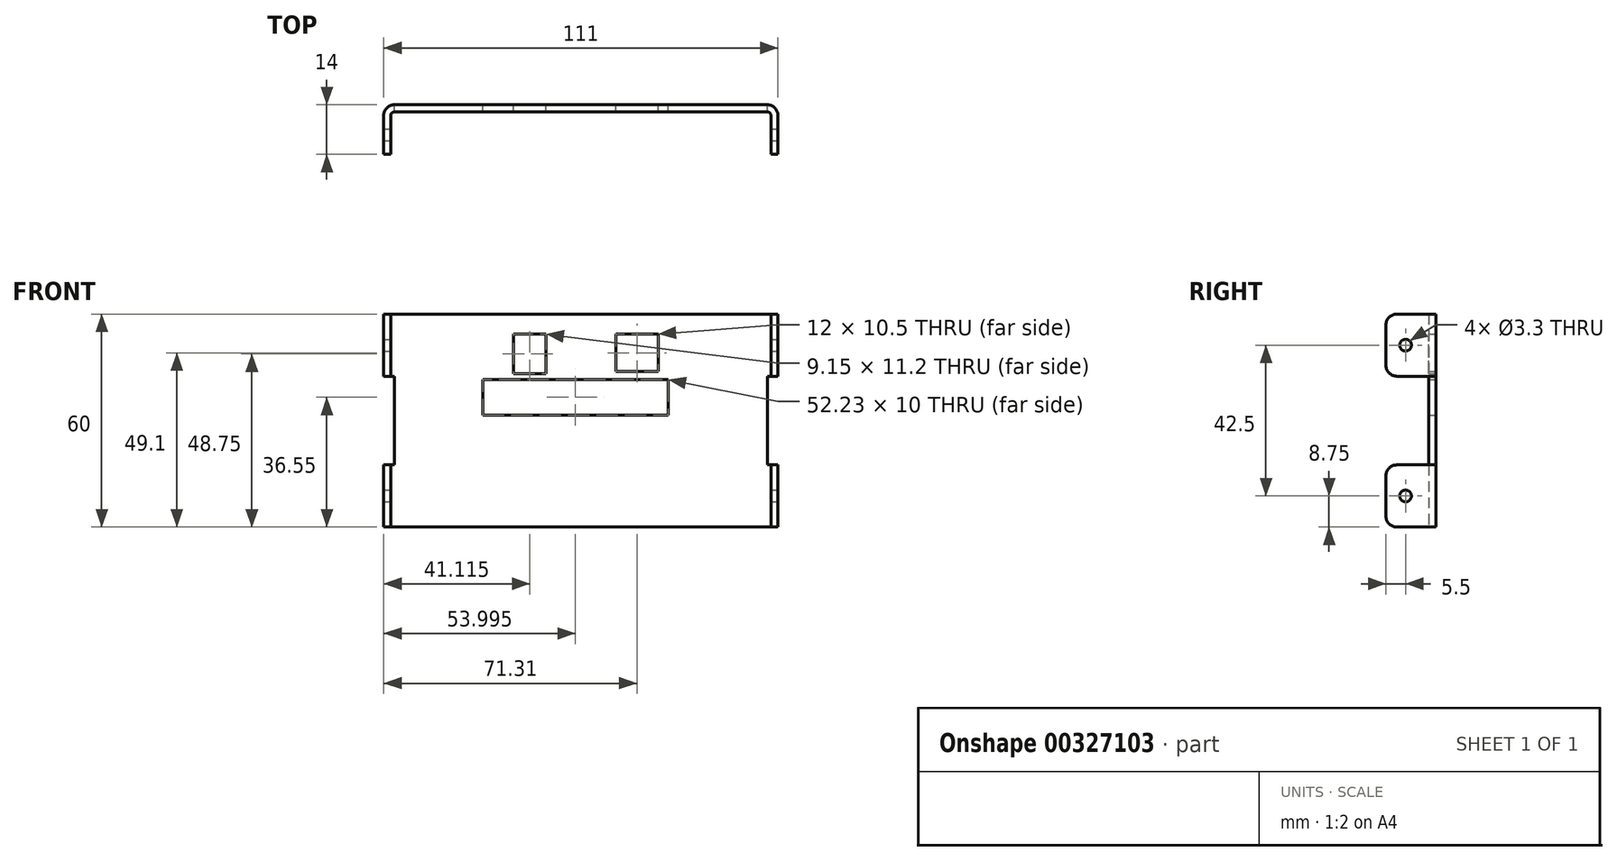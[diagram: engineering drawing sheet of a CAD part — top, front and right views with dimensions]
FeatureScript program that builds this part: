
annotation { "Feature Type Name" : "Feature", "Feature Type Description" : "" }
export const myFeature = defineFeature(function(context is Context, id is Id, definition is map)
    precondition{}
    {
        {
            var Q0;
            Q0=qCreatedBy(makeId("Top.planeOp"),FACE);
            var sketch = newSketch(context, id + "F0", { "sketchPlane" : qUnion([Q0])});
            skLineSegment(sketch, "E0", {"start": v(52.5, 0) * mm, "end": v(-52.5, 0) * mm});
            skLineSegment(sketch, "E1", {"start": v(-53.5, -1) * mm, "end": v(-53.5, -12) * mm});
            skLineSegment(sketch, "E2", {"start": v(53.5, -1) * mm, "end": v(53.5, -12) * mm});
            skPoint(sketch, "E3", {"position": v(0, 0) * mm});
            skPoint(sketch, "E4.visualSharp", {"position": v(-53.5, 0) * mm});
            skArc(sketch, "E4.filletArc", {"start": v(-52.5, 0) * mm, "mid": v(-53.2, -0.3) * mm, "end": v(-53.5, -1) * mm});
            skPoint(sketch, "E5.visualSharp", {"position": v(53.5, 0) * mm});
            skArc(sketch, "E5.filletArc", {"start": v(53.5, -1) * mm, "mid": v(53.2, -0.3) * mm, "end": v(52.5, 0) * mm});
            skLineSegment(sketch, "E6.0", {"start": v(-55.5, -1) * mm, "end": v(-55.5, -12) * mm});
            skLineSegment(sketch, "E6.1", {"start": v(55.5, -1) * mm, "end": v(55.5, -12) * mm});
            skArc(sketch, "E6.2", {"start": v(55.5, -1) * mm, "mid": v(54.62, 1.12) * mm, "end": v(52.5, 2) * mm});
            skLineSegment(sketch, "E6.3", {"start": v(52.5, 2) * mm, "end": v(-52.5, 2) * mm});
            skArc(sketch, "E6.4", {"start": v(-52.5, 2) * mm, "mid": v(-54.62, 1.12) * mm, "end": v(-55.5, -1) * mm});
            skLineSegment(sketch, "E7", {"start": v(-55.5, -12) * mm, "end": v(-53.5, -12) * mm});
            skLineSegment(sketch, "E8", {"start": v(53.5, -12) * mm, "end": v(55.5, -12) * mm});
            skSolve(sketch);
        }
        {
            var Q0;
            Q0=makeQuery(id+"F0.imprint","IMPRINT",FACE,{"disambiguationData":[TD([[makeQuery(id+"F0.imprint","IMPRINT",EDGE,{"derivedFrom":sQuery(id+"F0.wireOp",EDGE,"E0")}),-1.0]])]});
            extrude(context, id + "F1", {"entities" : qUnion([Q0]), "depth" : 60 * mm, "symmetric" : true});
        }
        {
            var Q0;
            Q0=makeQuery(id+"F1.opExtrude","SWEPT_FACE",FACE,{"disambiguationData":[OSD([sQuery(id+"F0.wireOp",EDGE,"E6.3")])]});
            var sketch = newSketch(context, id + "F2", { "sketchPlane" : qUnion([Q0])});
            skLineSegment(sketch, "E9.0", {"start": v(-55.5, 30) * mm, "end": v(-55.5, -30) * mm, "construction": true});
            skLineSegment(sketch, "E10.0", {"start": v(55.5, 30) * mm, "end": v(55.5, -30) * mm, "construction": true});
            skLineSegment(sketch, "E11.bottom", {"start": v(-55.5, 12.5) * mm, "end": v(-52.5, 12.5) * mm});
            skLineSegment(sketch, "E11.top", {"start": v(-55.5, -12.5) * mm, "end": v(-52.5, -12.5) * mm});
            skLineSegment(sketch, "E11.left", {"start": v(-55.5, 12.5) * mm, "end": v(-55.5, -12.5) * mm});
            skLineSegment(sketch, "E11.right", {"start": v(-52.5, 12.5) * mm, "end": v(-52.5, -12.5) * mm});
            skPoint(sketch, "E12", {"position": v(-52.5, 0) * mm});
            skLineSegment(sketch, "E13", {"start": v(0, 0) * mm, "end": v(0, 30) * mm, "construction": true});
            skLineSegment(sketch, "E14.MirrorCS", {"start": v(55.5, 12.5) * mm, "end": v(52.5, 12.5) * mm});
            skLineSegment(sketch, "E15.MirrorCS", {"start": v(55.5, -12.5) * mm, "end": v(52.5, -12.5) * mm});
            skPoint(sketch, "E16.MirrorP", {"position": v(52.5, 0) * mm});
            skLineSegment(sketch, "E17.MirrorCS", {"start": v(55.5, 12.5) * mm, "end": v(55.5, -12.5) * mm});
            skLineSegment(sketch, "E18.MirrorCS", {"start": v(52.5, 12.5) * mm, "end": v(52.5, -12.5) * mm});
            skLineSegment(sketch, "E19", {"start": v(-17.5, 26) * mm, "end": v(17.5, 26) * mm, "construction": true});
            skPoint(sketch, "E20", {"position": v(0, 26) * mm});
            skLineSegment(sketch, "E21.bottom", {"start": v(-21.81, 24.35) * mm, "end": v(-9.8, 24.35) * mm});
            skLineSegment(sketch, "E21.top", {"start": v(-21.81, 13.85) * mm, "end": v(-9.8, 13.85) * mm});
            skLineSegment(sketch, "E21.left", {"start": v(-21.81, 24.35) * mm, "end": v(-21.81, 13.85) * mm});
            skLineSegment(sketch, "E21.right", {"start": v(-9.8, 24.35) * mm, "end": v(-9.8, 13.85) * mm});
            skLineSegment(sketch, "E22.bottom", {"start": v(9.8, 24.35) * mm, "end": v(18.96, 24.35) * mm});
            skLineSegment(sketch, "E22.top", {"start": v(9.81, 13.15) * mm, "end": v(18.96, 13.15) * mm});
            skLineSegment(sketch, "E22.left", {"start": v(9.8, 24.35) * mm, "end": v(9.81, 13.15) * mm});
            skLineSegment(sketch, "E22.right", {"start": v(18.96, 24.35) * mm, "end": v(18.96, 13.15) * mm});
            skLineSegment(sketch, "E23", {"start": v(9.8, 24.35) * mm, "end": v(-9.8, 24.35) * mm, "construction": true});
            skPoint(sketch, "E24", {"position": v(0, 24.35) * mm});
            skLineSegment(sketch, "E25.bottom", {"start": v(-24.61, 11.55) * mm, "end": v(27.62, 11.55) * mm});
            skLineSegment(sketch, "E25.top", {"start": v(-24.61, 1.55) * mm, "end": v(27.62, 1.55) * mm});
            skLineSegment(sketch, "E25.left", {"start": v(-24.61, 11.55) * mm, "end": v(-24.61, 1.55) * mm});
            skLineSegment(sketch, "E25.right", {"start": v(27.62, 11.55) * mm, "end": v(27.62, 1.55) * mm});
            skSolve(sketch);
        }
        {
            var Q0;
            Q0=makeQuery(id+"F2.imprint","IMPRINT",FACE,{"disambiguationData":[TD([[makeQuery(id+"F2.imprint","IMPRINT",EDGE,{"derivedFrom":sQuery(id+"F2.wireOp",EDGE,"E11.bottom")}),-1.0]])]});
            var Q1;
            Q1=makeQuery(id+"F2.imprint","IMPRINT",FACE,{"disambiguationData":[TD([[makeQuery(id+"F2.imprint","IMPRINT",EDGE,{"derivedFrom":sQuery(id+"F2.wireOp",EDGE,"E14.MirrorCS")}),1.0]])]});
            var Q2;
            Q2=makeQuery(id+"F2.imprint","IMPRINT",FACE,{"disambiguationData":[TD([[makeQuery(id+"F2.imprint","IMPRINT",EDGE,{"derivedFrom":sQuery(id+"F2.wireOp",EDGE,"E21.bottom")}),-1.0]])]});
            var Q3;
            Q3=makeQuery(id+"F2.imprint","IMPRINT",FACE,{"disambiguationData":[TD([[makeQuery(id+"F2.imprint","IMPRINT",EDGE,{"derivedFrom":sQuery(id+"F2.wireOp",EDGE,"E22.bottom")}),-1.0]])]});
            var Q4;
            Q4=makeQuery(id+"F2.imprint","IMPRINT",FACE,{"disambiguationData":[TD([[makeQuery(id+"F2.imprint","IMPRINT",EDGE,{"derivedFrom":sQuery(id+"F2.wireOp",EDGE,"E25.bottom")}),-1.0]])]});
            extrude(context, id + "F3", {"entities" : qUnion([Q0, Q1, Q2, Q3, Q4]), "operationType" : NewBodyOperationType.REMOVE, "endBound" : BoundingType.THROUGH_ALL, "oppositeDirection" : true, "depth" : 25 * mm});
        }
        {
            var Q0;
            {var subQ2=sQuery(id+"F0.wireOp",EDGE,"E6.1");Q0=makeQuery(id+"F3.boolean.opBoolean","SPLIT",FACE,{"disambiguationData":[TD([makeQuery(id+"F3.opExtrude","SWEPT_FACE",FACE,{"disambiguationData":[OSD([sQuery(id+"F2.wireOp",EDGE,"E11.bottom")])]})])],"derivedFrom":makeQuery(id+"F1.opExtrude","SWEPT_FACE",FACE,{"disambiguationData":[OSD([subQ2])]})});}
            var sketch = newSketch(context, id + "F4", { "sketchPlane" : qUnion([Q0])});
            skLineSegment(sketch, "E26", {"start": v(-1, 12.5) * mm, "end": v(-12, 30) * mm, "construction": true});
            skLineSegment(sketch, "E27.0.0", {"start": v(-1, -12.5) * mm, "end": v(-12, -12.5) * mm, "construction": true});
            skLineSegment(sketch, "E27.0.1", {"start": v(-12, -12.5) * mm, "end": v(-12, -30) * mm, "construction": true});
            skLineSegment(sketch, "E27.0.2", {"start": v(-12, -30) * mm, "end": v(-1, -30) * mm, "construction": true});
            skLineSegment(sketch, "E27.0.3", {"start": v(-1, -30) * mm, "end": v(-1, -12.5) * mm, "construction": true});
            skLineSegment(sketch, "E28", {"start": v(-1, -30) * mm, "end": v(-12, -12.5) * mm, "construction": true});
            skPoint(sketch, "E29", {"position": v(-6.5, 21.25) * mm});
            skPoint(sketch, "E30", {"position": v(-6.5, -21.25) * mm});
            skSolve(sketch);
        }
        {
            var Q0;
            Q0=sQuery(id+"F4.wireOp",VERTEX,"E29");
            var Q1;
            Q1=sQuery(id+"F4.wireOp",VERTEX,"E30");
            var Q2;
            Q2=makeQuery(id+"F1.opExtrude","SWEPT_BODY",BODY,{"disambiguationData":[OSD([sQuery(id+"F0.wireOp",EDGE,"E0"),sQuery(id+"F0.wireOp",EDGE,"E1"),sQuery(id+"F0.wireOp",EDGE,"E2"),sQuery(id+"F0.wireOp",EDGE,"E4.filletArc"),sQuery(id+"F0.wireOp",EDGE,"E5.filletArc"),sQuery(id+"F0.wireOp",EDGE,"E6.0"),sQuery(id+"F0.wireOp",EDGE,"E6.1"),sQuery(id+"F0.wireOp",EDGE,"E6.2"),sQuery(id+"F0.wireOp",EDGE,"E6.3"),sQuery(id+"F0.wireOp",EDGE,"E6.4"),sQuery(id+"F0.wireOp",EDGE,"E7"),sQuery(id+"F0.wireOp",EDGE,"E8")])]});
            hole(context, id + "F5", {"style" : HoleStyle.SIMPLE, "endStyle" : HoleEndStyle.THROUGH, "standardTappedOrClearance" : lookupTablePath({ "standard" : "ISO", "fit" : "Normal", "size" : "M3", "type" : "Clearance" }), "standardBlindInLast" : lookupTablePath({ "fit" : "Standard", "standard" : "ISO", "size" : "M3", "type" : "Clearance" }), "holeDiameter" : 3.3 * mm, "tappedDepth" : 12 * mm, "tapClearance" : 3, "locations" : qUnion([Q0, Q1]), "scope" : qUnion([Q2])});
        }
        {
            var Q0;
            Q0=makeQuery(id+"F1.opExtrude","CAP_EDGE",EDGE,{"disambiguationData":[OSD([sQuery(id+"F0.wireOp",EDGE,"E7")])],"isStart":false});
            var Q1;
            Q1=makeQuery(id+"F3.boolean.opBoolean","INTERSECT",EDGE,{"derivedFrom":[makeQuery(id+"F1.opExtrude","SWEPT_FACE",FACE,{"disambiguationData":[OSD([sQuery(id+"F0.wireOp",EDGE,"E7")])]}),makeQuery(id+"F3.opExtrude","SWEPT_FACE",FACE,{"disambiguationData":[OSD([sQuery(id+"F2.wireOp",EDGE,"E14.MirrorCS")])]})]});
            var Q2;
            Q2=makeQuery(id+"F3.boolean.opBoolean","INTERSECT",EDGE,{"derivedFrom":[makeQuery(id+"F1.opExtrude","SWEPT_FACE",FACE,{"disambiguationData":[OSD([sQuery(id+"F0.wireOp",EDGE,"E7")])]}),makeQuery(id+"F3.opExtrude","SWEPT_FACE",FACE,{"disambiguationData":[OSD([sQuery(id+"F2.wireOp",EDGE,"E15.MirrorCS")])]})]});
            var Q3;
            Q3=makeQuery(id+"F1.opExtrude","CAP_EDGE",EDGE,{"disambiguationData":[OSD([sQuery(id+"F0.wireOp",EDGE,"E7")])],"isStart":true});
            var Q4;
            Q4=makeQuery(id+"F1.opExtrude","CAP_EDGE",EDGE,{"disambiguationData":[OSD([sQuery(id+"F0.wireOp",EDGE,"E8")])],"isStart":false});
            var Q5;
            Q5=makeQuery(id+"F3.boolean.opBoolean","INTERSECT",EDGE,{"derivedFrom":[makeQuery(id+"F1.opExtrude","SWEPT_FACE",FACE,{"disambiguationData":[OSD([sQuery(id+"F0.wireOp",EDGE,"E8")])]}),makeQuery(id+"F3.opExtrude","SWEPT_FACE",FACE,{"disambiguationData":[OSD([sQuery(id+"F2.wireOp",EDGE,"E11.bottom")])]})]});
            var Q6;
            Q6=makeQuery(id+"F3.boolean.opBoolean","INTERSECT",EDGE,{"derivedFrom":[makeQuery(id+"F1.opExtrude","SWEPT_FACE",FACE,{"disambiguationData":[OSD([sQuery(id+"F0.wireOp",EDGE,"E8")])]}),makeQuery(id+"F3.opExtrude","SWEPT_FACE",FACE,{"disambiguationData":[OSD([sQuery(id+"F2.wireOp",EDGE,"E11.top")])]})]});
            var Q7;
            Q7=makeQuery(id+"F1.opExtrude","CAP_EDGE",EDGE,{"disambiguationData":[OSD([sQuery(id+"F0.wireOp",EDGE,"E8")])],"isStart":true});
            fillet(context, id + "F6", {"entities" : qUnion([Q0, Q1, Q2, Q3, Q4, Q5, Q6, Q7]), "radius" : 3 * mm, "tangentPropagation" : true, "allowEdgeOverflow" : false});
        }
    });
